FCSTD DOCUMENT  (FreeCAD 1.0R39319 (Git))
Label: Base_Rocher
License: All rights reserved
LicenseURL: http://en.wikipedia.org/wiki/All_rights_reserved
objects: Sketcher::SketchObject×1, PartDesign::Body×1, TechDraw::DrawSVGTemplate×1, TechDraw::DrawProjGroupItem×1, TechDraw::DrawPage×1
note: 3 computed .brp shape members not serialized (recipe doc carries the construction recipe); baked Part::Feature solids carry a one-line shape summary decoded from their .brp

FEATURE [Sketcher::SketchObject] Sketch
  ArcFitTolerance = 1e-06
  AttachmentSupport = -> [XY_Plane]
  FullyConstrained = false
  MakeInternals = false
  MapMode = 5
  sketch-geometry (128):
    g0: Circle CenterX=-3e-16 CenterY=1.1e-15 CenterZ=0 NormalX=0 NormalY=0 NormalZ=1 AngleXU=0 Radius=65
    g1: LineSegment StartX=-47.7671 StartY=7.5 StartZ=0 EndX=-47.7671 EndY=-7.5 EndZ=0
    g2: LineSegment StartX=-47.7671 StartY=-7.5 StartZ=0 EndX=-38.7671 EndY=-7.5 EndZ=0
    g3: LineSegment StartX=-38.7671 StartY=-7.5 StartZ=0 EndX=-38.7671 EndY=7.5 EndZ=0
    g4: LineSegment StartX=-38.7671 StartY=7.5 StartZ=0 EndX=-47.7671 EndY=7.5 EndZ=0
    g5: LineSegment [constr] StartX=-88.9375 StartY=57.8248 StartZ=0 EndX=57.8248 EndY=-88.9375 EndZ=0
    g6: LineSegment [constr] StartX=57.8248 StartY=-88.9375 StartZ=0 EndX=88.9375 EndY=-57.8248 EndZ=0
    g7: LineSegment [constr] StartX=88.9375 StartY=-57.8248 StartZ=0 EndX=-57.8248 EndY=88.9375 EndZ=0
    g8: LineSegment [constr] StartX=-57.8248 StartY=88.9375 StartZ=0 EndX=-88.9375 EndY=57.8248 EndZ=0
    g9: GeomPoint [constr] X=15.5563 Y=15.5563 Z=0
    g10: GeomPoint [constr] X=-15.5563 Y=-15.5563 Z=0
    g11: LineSegment [constr] StartX=-60.7671 StartY=21 StartZ=0 EndX=-60.7671 EndY=-21 EndZ=0
    g12: LineSegment [constr] StartX=-60.7671 StartY=-21 StartZ=0 EndX=-45.7671 EndY=-21 EndZ=0
    g13: LineSegment [constr] StartX=-45.7671 StartY=-21 StartZ=0 EndX=-45.7671 EndY=21 EndZ=0
    g14: LineSegment [constr] StartX=-45.7671 StartY=21 StartZ=0 EndX=-60.7671 EndY=21 EndZ=0
    g15: GeomPoint [constr] X=-60.7671 Y=0 Z=0
    g16: Circle CenterX=-53.2671 CenterY=18.2545 CenterZ=0 NormalX=0 NormalY=0 NormalZ=1 AngleXU=0 Radius=0.75
    g17: Circle CenterX=-57.0171 CenterY=13.0749 CenterZ=0 NormalX=0 NormalY=0 NormalZ=1 AngleXU=0 Radius=0.75
    g18: Circle CenterX=-49.5171 CenterY=13.0749 CenterZ=0 NormalX=0 NormalY=0 NormalZ=1 AngleXU=0 Radius=0.75
    g19: Circle CenterX=-57.0171 CenterY=-13.0749 CenterZ=0 NormalX=0 NormalY=0 NormalZ=1 AngleXU=0 Radius=0.75
    g20: Circle CenterX=-49.5171 CenterY=-13.0749 CenterZ=0 NormalX=0 NormalY=0 NormalZ=1 AngleXU=0 Radius=0.75
    g21: Circle CenterX=-53.2671 CenterY=-18.2545 CenterZ=0 NormalX=0 NormalY=0 NormalZ=1 AngleXU=0 Radius=0.75
    g22: LineSegment [constr] StartX=-57.0171 StartY=13.0749 StartZ=0 EndX=-49.5171 EndY=13.0749 EndZ=0
    g23: GeomPoint [constr] X=-53.2671 Y=13.0749 Z=0
    g24: GeomPoint [constr] X=-53.2671 Y=-21 Z=0
    g25: GeomPoint [constr] X=15.5563 Y=-15.5563 Z=0
    g26: GeomPoint [constr] X=-15.5563 Y=15.5563 Z=0
    g27: LineSegment StartX=0 StartY=9.34827 StartZ=0 EndX=0 EndY=-10.2987 EndZ=0
    g28: LineSegment StartX=-10.3651 StartY=0 StartZ=0 EndX=9.28182 EndY=0 EndZ=0
    g29: GeomPoint [constr] X=-38.7671 Y=0 Z=0
    g30: LineSegment [constr] StartX=-57.0171 StartY=13.0749 StartZ=0 EndX=-57.0171 EndY=-13.0749 EndZ=0
    g31: GeomPoint [constr] X=-57.0171 Y=0 Z=0
    g32: LineSegment StartX=7.5 StartY=47.7671 StartZ=0 EndX=-7.5 EndY=47.7671 EndZ=0
    g33: LineSegment StartX=-7.5 StartY=47.7671 StartZ=0 EndX=-7.5 EndY=38.7671 EndZ=0
    g34: LineSegment StartX=-7.5 StartY=38.7671 StartZ=0 EndX=7.5 EndY=38.7671 EndZ=0
    g35: LineSegment StartX=7.5 StartY=38.7671 StartZ=0 EndX=7.5 EndY=47.7671 EndZ=0
    g36: LineSegment [constr] StartX=21 StartY=60.7671 StartZ=0 EndX=-21 EndY=60.7671 EndZ=0
    g37: LineSegment [constr] StartX=-21 StartY=60.7671 StartZ=0 EndX=-21 EndY=45.7671 EndZ=0
    g38: LineSegment [constr] StartX=-21 StartY=45.7671 StartZ=0 EndX=21 EndY=45.7671 EndZ=0
    g39: LineSegment [constr] StartX=21 StartY=45.7671 StartZ=0 EndX=21 EndY=60.7671 EndZ=0
    g40: GeomPoint [constr] X=0 Y=60.7671 Z=0
    g41: Circle CenterX=18.2545 CenterY=53.2671 CenterZ=0 NormalX=0 NormalY=0 NormalZ=1 AngleXU=0 Radius=0.75
    g42: Circle CenterX=13.0749 CenterY=57.0171 CenterZ=0 NormalX=0 NormalY=0 NormalZ=1 AngleXU=0 Radius=0.75
    g43: Circle CenterX=13.0749 CenterY=49.5171 CenterZ=0 NormalX=0 NormalY=0 NormalZ=1 AngleXU=0 Radius=0.75
    g44: Circle CenterX=-13.0749 CenterY=57.0171 CenterZ=0 NormalX=0 NormalY=0 NormalZ=1 AngleXU=0 Radius=0.75
    g45: Circle CenterX=-13.0749 CenterY=49.5171 CenterZ=0 NormalX=0 NormalY=0 NormalZ=1 AngleXU=0 Radius=0.75
    g46: Circle CenterX=-18.2545 CenterY=53.2671 CenterZ=0 NormalX=0 NormalY=0 NormalZ=1 AngleXU=0 Radius=0.75
    g47: LineSegment [constr] StartX=13.0749 StartY=57.0171 StartZ=0 EndX=13.0749 EndY=49.5171 EndZ=0
    g48: GeomPoint [constr] X=13.0749 Y=53.2671 Z=0
    g49: GeomPoint [constr] X=-21 Y=53.2671 Z=0
    g50: GeomPoint [constr] X=0 Y=38.7671 Z=0
    g51: LineSegment [constr] StartX=13.0749 StartY=57.0171 StartZ=0 EndX=-13.0749 EndY=57.0171 EndZ=0
    g52: GeomPoint [constr] X=0 Y=57.0171 Z=0
    g53: LineSegment StartX=47.7671 StartY=-7.5 StartZ=0 EndX=47.7671 EndY=7.5 EndZ=0
    g54: LineSegment StartX=47.7671 StartY=7.5 StartZ=0 EndX=38.7671 EndY=7.5 EndZ=0
    g55: LineSegment StartX=38.7671 StartY=7.5 StartZ=0 EndX=38.7671 EndY=-7.5 EndZ=0
    g56: LineSegment StartX=38.7671 StartY=-7.5 StartZ=0 EndX=47.7671 EndY=-7.5 EndZ=0
    g57: LineSegment [constr] StartX=60.7671 StartY=-21 StartZ=0 EndX=60.7671 EndY=21 EndZ=0
    g58: LineSegment [constr] StartX=60.7671 StartY=21 StartZ=0 EndX=45.7671 EndY=21 EndZ=0
    g59: LineSegment [constr] StartX=45.7671 StartY=21 StartZ=0 EndX=45.7671 EndY=-21 EndZ=0
    g60: LineSegment [constr] StartX=45.7671 StartY=-21 StartZ=0 EndX=60.7671 EndY=-21 EndZ=0
    g61: GeomPoint [constr] X=60.7671 Y=0 Z=0
    g62: Circle CenterX=53.2671 CenterY=-18.2545 CenterZ=0 NormalX=0 NormalY=0 NormalZ=1 AngleXU=0 Radius=0.75
    g63: Circle CenterX=57.0171 CenterY=-13.0749 CenterZ=0 NormalX=0 NormalY=0 NormalZ=1 AngleXU=0 Radius=0.75
    g64: Circle CenterX=49.5171 CenterY=-13.0749 CenterZ=0 NormalX=0 NormalY=0 NormalZ=1 AngleXU=0 Radius=0.75
    g65: Circle CenterX=57.0171 CenterY=13.0749 CenterZ=0 NormalX=0 NormalY=0 NormalZ=1 AngleXU=0 Radius=0.75
    g66: Circle CenterX=49.5171 CenterY=13.0749 CenterZ=0 NormalX=0 NormalY=0 NormalZ=1 AngleXU=0 Radius=0.75
    g67: Circle CenterX=53.2671 CenterY=18.2545 CenterZ=0 NormalX=0 NormalY=0 NormalZ=1 AngleXU=0 Radius=0.75
    g68: LineSegment [constr] StartX=57.0171 StartY=-13.0749 StartZ=0 EndX=49.5171 EndY=-13.0749 EndZ=0
    g69: GeomPoint [constr] X=53.2671 Y=-13.0749 Z=0
    g70: GeomPoint [constr] X=53.2671 Y=21 Z=0
    g71: GeomPoint [constr] X=38.7671 Y=0 Z=0
    g72: LineSegment [constr] StartX=57.0171 StartY=-13.0749 StartZ=0 EndX=57.0171 EndY=13.0749 EndZ=0
    g73: GeomPoint [constr] X=57.0171 Y=0 Z=0
    g74: LineSegment StartX=-7.5 StartY=-47.7671 StartZ=0 EndX=7.5 EndY=-47.7671 EndZ=0
    g75: LineSegment StartX=7.5 StartY=-47.7671 StartZ=0 EndX=7.5 EndY=-38.7671 EndZ=0
    g76: LineSegment StartX=7.5 StartY=-38.7671 StartZ=0 EndX=-7.5 EndY=-38.7671 EndZ=0
    g77: LineSegment StartX=-7.5 StartY=-38.7671 StartZ=0 EndX=-7.5 EndY=-47.7671 EndZ=0
    g78: LineSegment [constr] StartX=-21 StartY=-60.7671 StartZ=0 EndX=21 EndY=-60.7671 EndZ=0
    g79: LineSegment [constr] StartX=21 StartY=-60.7671 StartZ=0 EndX=21 EndY=-45.7671 EndZ=0
    g80: LineSegment [constr] StartX=21 StartY=-45.7671 StartZ=0 EndX=-21 EndY=-45.7671 EndZ=0
    g81: LineSegment [constr] StartX=-21 StartY=-45.7671 StartZ=0 EndX=-21 EndY=-60.7671 EndZ=0
    g82: GeomPoint [constr] X=0 Y=-60.7671 Z=0
    g83: Circle CenterX=-18.2545 CenterY=-53.2671 CenterZ=0 NormalX=0 NormalY=0 NormalZ=1 AngleXU=0 Radius=0.75
    g84: Circle CenterX=-13.0749 CenterY=-57.0171 CenterZ=0 NormalX=0 NormalY=0 NormalZ=1 AngleXU=0 Radius=0.75
    g85: Circle CenterX=-13.0749 CenterY=-49.5171 CenterZ=0 NormalX=0 NormalY=0 NormalZ=1 AngleXU=0 Radius=0.75
    g86: Circle CenterX=13.0749 CenterY=-57.0171 CenterZ=0 NormalX=0 NormalY=0 NormalZ=1 AngleXU=0 Radius=0.75
    g87: Circle CenterX=13.0749 CenterY=-49.5171 CenterZ=0 NormalX=0 NormalY=0 NormalZ=1 AngleXU=0 Radius=0.75
    g88: Circle CenterX=18.2545 CenterY=-53.2671 CenterZ=0 NormalX=0 NormalY=0 NormalZ=1 AngleXU=0 Radius=0.75
    g89: LineSegment [constr] StartX=-13.0749 StartY=-57.0171 StartZ=0 EndX=-13.0749 EndY=-49.5171 EndZ=0
    g90: GeomPoint [constr] X=-13.0749 Y=-53.2671 Z=0
    g91: GeomPoint [constr] X=21 Y=-53.2671 Z=0
    g92: GeomPoint [constr] X=0 Y=-38.7671 Z=0
    g93: LineSegment [constr] StartX=-13.0749 StartY=-57.0171 StartZ=0 EndX=13.0749 EndY=-57.0171 EndZ=0
    g94: GeomPoint [constr] X=0 Y=-57.0171 Z=0
    g95: GeomPoint [constr] X=-46.0514 Y=-30.9568 Z=0
    g96: GeomPoint [constr] X=-31.4861 Y=-46.5806 Z=0
    g97: LineSegment [constr] StartX=-46.0514 StartY=-30.9568 StartZ=0 EndX=-31.4861 EndY=-46.5806 EndZ=0
    g98: LineSegment [constr] StartX=-3e-16 StartY=1.1e-15 StartZ=0 EndX=-54.3037 EndY=-54.3037 EndZ=0
    g99: GeomPoint [constr] X=-38.7687 Y=-38.7687 Z=0
    g100: Circle CenterX=-46.0514 CenterY=-30.9568 CenterZ=0 NormalX=0 NormalY=0 NormalZ=1 AngleXU=0 Radius=1.3e-15
    g101: Circle CenterX=-31.4861 CenterY=-46.5806 CenterZ=0 NormalX=0 NormalY=0 NormalZ=1 AngleXU=0 Radius=1.7e-15
    g102: Circle CenterX=-46.0514 CenterY=-30.9568 CenterZ=0 NormalX=0 NormalY=0 NormalZ=1 AngleXU=0 Radius=0.8
    g103: Circle CenterX=-31.4861 CenterY=-46.5806 CenterZ=0 NormalX=0 NormalY=0 NormalZ=1 AngleXU=0 Radius=0.8
    g104: GeomPoint [constr] X=-30.9573 Y=46.051 Z=0
    g105: GeomPoint [constr] X=-46.5802 Y=31.4865 Z=0
    g106: LineSegment [constr] StartX=-30.9573 StartY=46.051 StartZ=0 EndX=-46.5802 EndY=31.4865 EndZ=0
    g107: GeomPoint [constr] X=-38.7687 Y=38.7687 Z=0
    g108: Circle CenterX=-30.9573 CenterY=46.051 CenterZ=0 NormalX=0 NormalY=0 NormalZ=1 AngleXU=0 Radius=0
    g109: Circle CenterX=-46.5802 CenterY=31.4865 CenterZ=0 NormalX=0 NormalY=0 NormalZ=1 AngleXU=0 Radius=0
    g110: Circle CenterX=-30.9573 CenterY=46.051 CenterZ=0 NormalX=0 NormalY=0 NormalZ=1 AngleXU=0 Radius=0.8
    g111: Circle CenterX=-46.5802 CenterY=31.4865 CenterZ=0 NormalX=0 NormalY=0 NormalZ=1 AngleXU=0 Radius=0.8
    g112: GeomPoint [constr] X=46.051 Y=30.9573 Z=0
    g113: GeomPoint [constr] X=31.4865 Y=46.5802 Z=0
    g114: LineSegment [constr] StartX=46.051 StartY=30.9573 StartZ=0 EndX=31.4865 EndY=46.5802 EndZ=0
    g115: GeomPoint [constr] X=38.7687 Y=38.7687 Z=0
    g116: Circle CenterX=46.051 CenterY=30.9573 CenterZ=0 NormalX=0 NormalY=0 NormalZ=1 AngleXU=0 Radius=0
    g117: Circle CenterX=31.4865 CenterY=46.5802 CenterZ=0 NormalX=0 NormalY=0 NormalZ=1 AngleXU=0 Radius=0
    g118: Circle CenterX=46.051 CenterY=30.9573 CenterZ=0 NormalX=0 NormalY=0 NormalZ=1 AngleXU=0 Radius=0.8
    g119: Circle CenterX=31.4865 CenterY=46.5802 CenterZ=0 NormalX=0 NormalY=0 NormalZ=1 AngleXU=0 Radius=0.8
    g120: GeomPoint [constr] X=30.9573 Y=-46.051 Z=0
    g121: GeomPoint [constr] X=46.5802 Y=-31.4865 Z=0
    g122: LineSegment [constr] StartX=30.9573 StartY=-46.051 StartZ=0 EndX=46.5802 EndY=-31.4865 EndZ=0
    g123: GeomPoint [constr] X=38.7687 Y=-38.7687 Z=0
    g124: Circle CenterX=30.9573 CenterY=-46.051 CenterZ=0 NormalX=0 NormalY=0 NormalZ=1 AngleXU=0 Radius=0
    g125: Circle CenterX=46.5802 CenterY=-31.4865 CenterZ=0 NormalX=0 NormalY=0 NormalZ=1 AngleXU=0 Radius=0
    g126: Circle CenterX=30.9573 CenterY=-46.051 CenterZ=0 NormalX=0 NormalY=0 NormalZ=1 AngleXU=0 Radius=0.8
    g127: Circle CenterX=46.5802 CenterY=-31.4865 CenterZ=0 NormalX=0 NormalY=0 NormalZ=1 AngleXU=0 Radius=0.8
  constraints (177):
    c: Coincident(g0,g-1)
    c: Coincident(g1,g2)
    c: Coincident(g2,g3)
    c: Coincident(g3,g4)
    c: Coincident(g4,g1)
    c: Vertical(g1)
    c: Horizontal(g2)
    c: Horizontal(g4)
    c: Distance(g3,g2) = 15
    c: DistanceX(g1,g2) = 9
    c: Symmetric(g3,g2,g-1)
    c: Coincident(g5,g6)
    c: Coincident(g6,g7)
    c: Coincident(g7,g8)
    c: Coincident(g8,g5)
    c: Angle(g5,g8) = 1.5708
    c: Angle(g7,g6) = 1.5708
    c: Angle(g8,g7) = 1.5708
    c: Angle(g-2,g7) = 0.785398
    c: Symmetric(g7,g7,g9)
    c: Symmetric(g5,g5,g10)
    c: Symmetric(g9,g10,g0)
    c: Diameter(g0) = 130
    c: Coincident(g11,g12)
    c: Coincident(g12,g13)
    c: Coincident(g13,g14)
    c: Coincident(g14,g11)
    c: Vertical(g11)
    c: Vertical(g13)
    c: Horizontal(g12)
    c: Horizontal(g14)
    c: Symmetric(g11,g11,g15)
    c: PointOnObject(g15,g-1)
    c: DistanceX(g12,g12) = 15
    c: DistanceY(g11,g11) = 42
    c: Equal(g17,g16)
    c: Equal(g16,g18)
    c: Equal(g18,g20)
    c: Equal(g20,g19)
    c: Equal(g19,g21)
    c: Symmetric(g17,g19,g-1)
    c: Symmetric(g18,g20,g-1)
    c: Symmetric(g21,g16,g-1)
    c: Coincident(g22,g17)
    c: Coincident(g22,g18)
    c: Symmetric(g22,g22,g23)
    c: Vertical(g23,g16)
    c: Horizontal(g18,g17)
    c: DistanceX(g17,g18) = 7.5
    c: DistanceY(g18,g16) = 5.17961
    c: DistanceY(g-1,g17) = 13.0749
    c: DistanceX(g1,g13) = 2
    c: Symmetric(g12,g12,g24)
    c: Vertical(g21,g24)
    c: Diameter(g21) = 1.5
    c: PointOnObject(g27,g-2)
    c: PointOnObject(g27,g-2)
    c: PointOnObject(g28,g-1)
    c: PointOnObject(g28,g-1)
    c: Equal(g28,g27)
    c: Symmetric(g3,g3,g29)
    c: Coincident(g30,g17)
    c: Coincident(g30,g19)
    c: Symmetric(g30,g30,g31)
    c: Distance(g5,g7) = 44
    c: Coincident(g32,g33)
    c: Coincident(g53,g54)
    c: Coincident(g74,g75)
    c: Coincident(g33,g34)
    c: Coincident(g54,g55)
    c: Coincident(g75,g76)
    c: Coincident(g34,g35)
    c: Coincident(g55,g56)
    c: Coincident(g76,g77)
    c: Coincident(g35,g32)
    c: Coincident(g56,g53)
    c: Coincident(g77,g74)
    c: Distance(g34,g33) = 15
    c: Distance(g55,g54) = 15
    c: Distance(g76,g75) = 15
    c: Coincident(g36,g37)
    c: Coincident(g57,g58)
    c: Coincident(g78,g79)
    c: Coincident(g37,g38)
    c: Coincident(g58,g59)
    c: Coincident(g79,g80)
    c: Coincident(g38,g39)
    c: Coincident(g59,g60)
    c: Coincident(g80,g81)
    c: Coincident(g39,g36)
    c: Coincident(g60,g57)
    c: Coincident(g81,g78)
    c: Symmetric(g36,g36,g40)
    c: Symmetric(g57,g57,g61)
    c: Symmetric(g78,g78,g82)
    c: Equal(g42,g41)
    c: Equal(g63,g62)
    c: Equal(g84,g83)
    c: Equal(g41,g43)
    c: Equal(g62,g64)
    c: Equal(g83,g85)
    c: Equal(g43,g45)
    c: Equal(g64,g66)
    c: Equal(g85,g87)
    c: Equal(g45,g44)
    c: Equal(g66,g65)
    c: Equal(g87,g86)
    c: Equal(g44,g46)
    c: Equal(g65,g67)
    c: Equal(g86,g88)
    c: Coincident(g47,g42)
    c: Coincident(g68,g63)
    c: Coincident(g89,g84)
    c: Coincident(g47,g43)
    c: Coincident(g68,g64)
    c: Coincident(g89,g85)
    c: Symmetric(g47,g47,g48)
    c: Symmetric(g68,g68,g69)
    c: Symmetric(g89,g89,g90)
    c: Symmetric(g37,g37,g49)
    c: Symmetric(g58,g58,g70)
    c: Symmetric(g79,g79,g91)
    c: Diameter(g46) = 1.5
    c: Diameter(g67) = 1.5
    c: Diameter(g88) = 1.5
    c: Symmetric(g34,g34,g50)
    c: Symmetric(g55,g55,g71)
    c: Symmetric(g76,g76,g92)
    c: Coincident(g51,g42)
    c: Coincident(g72,g63)
    c: Coincident(g93,g84)
    c: Coincident(g51,g44)
    c: Coincident(g72,g65)
    c: Coincident(g93,g86)
    c: Symmetric(g51,g51,g52)
    c: Symmetric(g72,g72,g73)
    c: Symmetric(g93,g93,g94)
    c: Coincident(g97,g95)
    c: Coincident(g97,g96)
    c: Coincident(g98,g0)
    c: Symmetric(g97,g97,g99)
    c: Coincident(g100,g95)
    c: Coincident(g101,g96)
    c: Coincident(g102,g95)
    c: Coincident(g103,g96)
    c: Equal(g102,g103)
    c: Diameter(g102) = 1.6
    c: PointOnObject(g99,g98)
    c: Angle(g98,g-1) = 2.35619
    c: Coincident(g106,g104)
    c: Coincident(g114,g112)
    c: Coincident(g122,g120)
    c: Coincident(g106,g105)
    c: Coincident(g114,g113)
    c: Coincident(g122,g121)
    c: Symmetric(g106,g106,g107)
    c: Symmetric(g114,g114,g115)
    c: Symmetric(g122,g122,g123)
    c: Coincident(g108,g104)
    c: Coincident(g116,g112)
    c: Coincident(g124,g120)
    c: Coincident(g109,g105)
    c: Coincident(g117,g113)
    c: Coincident(g125,g121)
    c: Coincident(g110,g104)
    c: Coincident(g118,g112)
    c: Coincident(g126,g120)
    c: Coincident(g111,g105)
    c: Coincident(g119,g113)
    c: Coincident(g127,g121)
    c: Equal(g110,g111)
    c: Equal(g118,g119)
    c: Equal(g126,g127)
    c: Diameter(g110) = 1.6
    c: Diameter(g118) = 1.6
    c: Diameter(g126) = 1.6
    c: Distance(g95,g96) = 21.36
FEATURE [PartDesign::Body] Body
  AllowCompound = false
  Group = -> [Sketch]
  Origin = -> Origin
FEATURE [TechDraw::DrawSVGTemplate] Template
  Height = 210
  Orientation = 1
  Template = <path>
  Width = 297
FEATURE [TechDraw::DrawProjGroupItem] View
  CoarseView = false
  Direction = (0,0,-1)
  Focus = 100
  HardHidden = false
  IsoCount = 0
  IsoHidden = false
  IsoVisible = false
  LockPosition = false
  Perspective = false
  Rotation = 0
  RotationVector = (1,0,0)
  ScaleType = 2
  ScrubCount = 1
  SeamHidden = false
  SeamVisible = false
  SmoothHidden = false
  SmoothVisible = true
  Source = -> [Sketch]
  Type = 0
  X = 148.5
  XDirection = (1,0,0)
  Y = 105
FEATURE [TechDraw::DrawPage] Page
  KeepUpdated = true
  NextBalloonIndex = 1
  ProjectionType = 0
  Template = -> Template
  Views = -> [View]
note: 1 file-system path scrubbed to <path> (originals preserved in the JSON sidecar)
